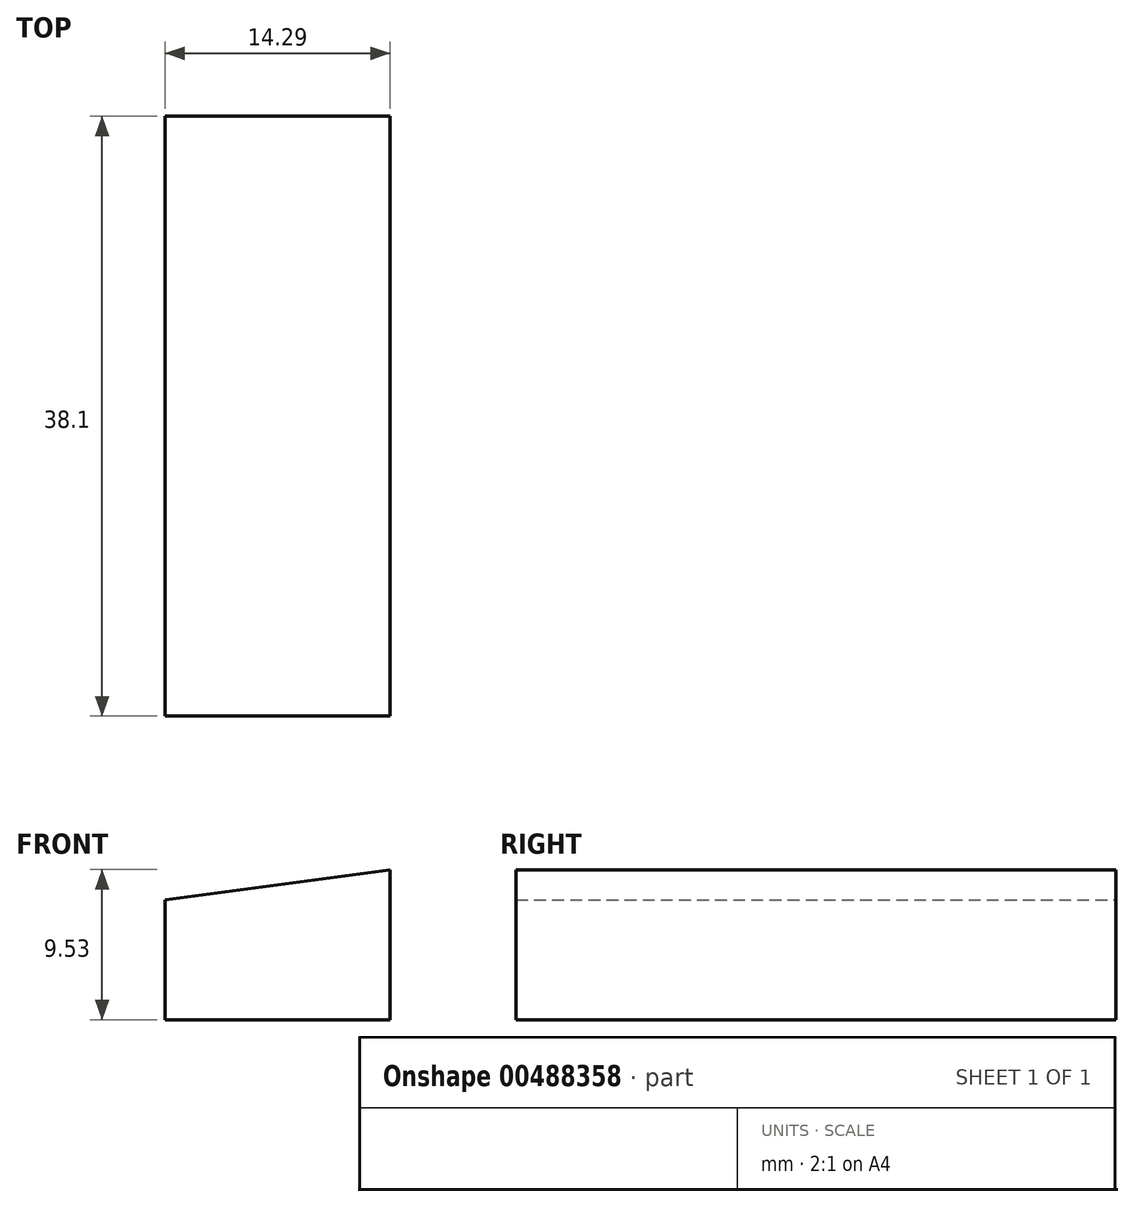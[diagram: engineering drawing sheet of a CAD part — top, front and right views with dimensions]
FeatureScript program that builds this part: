
annotation { "Feature Type Name" : "Feature", "Feature Type Description" : "" }
export const myFeature = defineFeature(function(context is Context, id is Id, definition is map)
    precondition{}
    {
        {
            var Q0;
            Q0=qCreatedBy(makeId("Front.planeOp"),FACE);
            var sketch = newSketch(context, id + "F0", { "sketchPlane" : qUnion([Q0])});
            skLineSegment(sketch, "E0", {"start": v(-2.98, 0) * mm, "end": v(-2.98, 7.62) * mm});
            skLineSegment(sketch, "E1", {"start": v(-2.98, 0) * mm, "end": v(11.3, 0) * mm});
            skLineSegment(sketch, "E2", {"start": v(11.3, 0) * mm, "end": v(11.3, 9.53) * mm});
            skLineSegment(sketch, "E3", {"start": v(11.3, 9.53) * mm, "end": v(-2.98, 7.62) * mm});
            skSolve(sketch);
        }
        {
            var Q0;
            Q0 = qSketchRegion(id + "F0", true);
            extrude(context, id + "F1", {"entities" : qUnion([Q0]), "depth" : 38.1 * mm});
        }
    });
